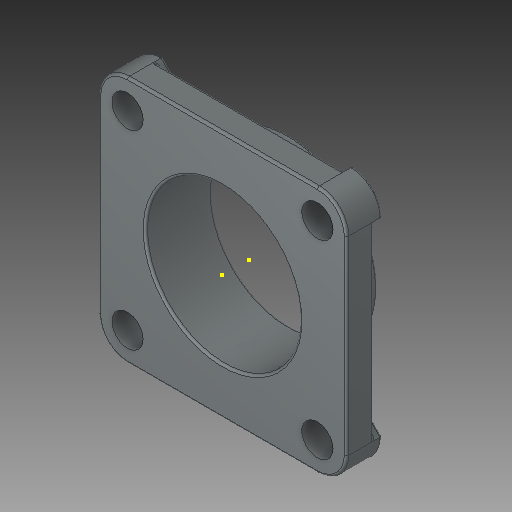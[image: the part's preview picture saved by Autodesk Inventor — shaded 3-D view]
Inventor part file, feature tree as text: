
AUTODESK INVENTOR PART (.ipt)
format: ipt  version: 2019 (Build 230136000, 136)  size: 446,464 bytes
history: native  units: in
note: dims shown in document units (in); Inventor stores cm internally (conversion verified against a paired STEP export)
features: sketch x10, other x3
ambient origin geometry x8: Origin, YZ Plane, XZ Plane, XY Plane, X Axis, Y Axis, Z Axis, Center Point
bodies: Solid1 (feature_tree)
feature tree (13):
  other  "project flange bearing part1.ipt"
  other  "Solid1::project flange bearing part1.ipt"
  other  "TaggingFeature1"
  sketch  "Sketch1"  dims[d0=0.3937in]
  sketch  "Sketch2"
  sketch  "Sketch3"
  sketch  "Sketch4"
  sketch  "Sketch5"
  sketch  "Sketch6"
  sketch  "Sketch7"
  sketch  "Sketch8"
  sketch  "Sketch9"
  sketch  "Sketch10"
